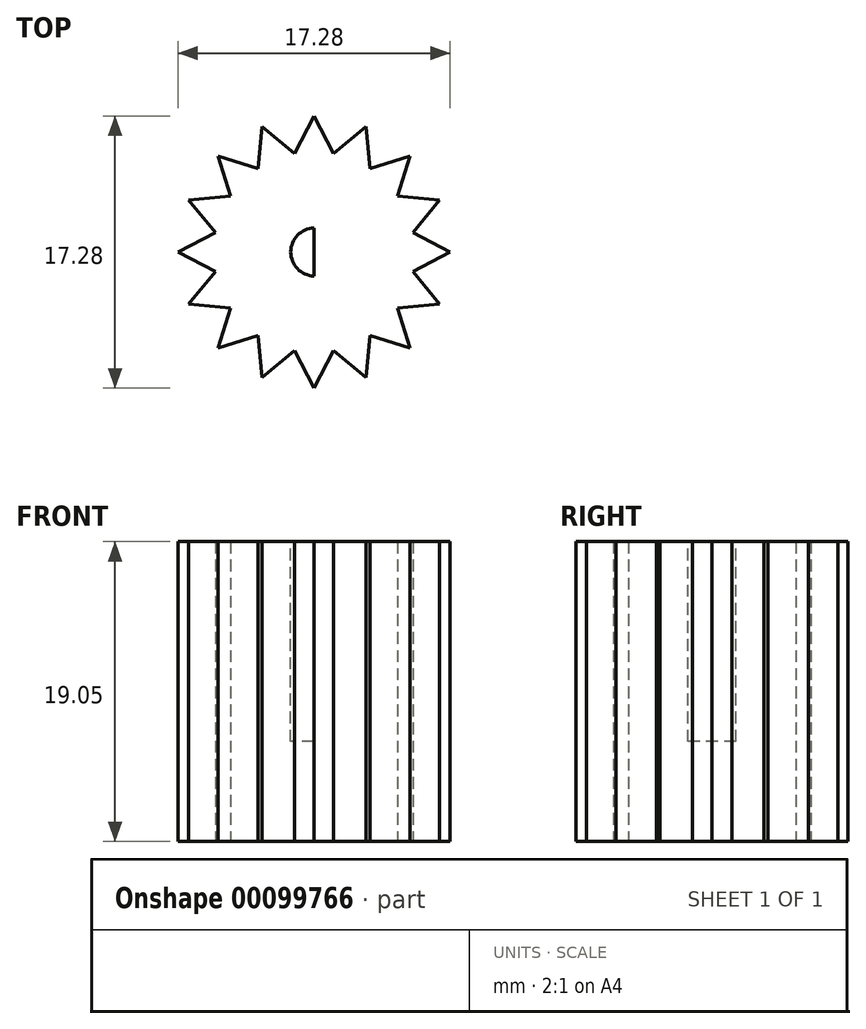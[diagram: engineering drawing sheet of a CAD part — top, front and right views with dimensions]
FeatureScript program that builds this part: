
annotation { "Feature Type Name" : "Feature", "Feature Type Description" : "" }
export const myFeature = defineFeature(function(context is Context, id is Id, definition is map)
    precondition{}
    {
        {
            var Q0;
            Q0=qCreatedBy(makeId("Top.planeOp"),FACE);
            var sketch = newSketch(context, id + "F0", { "sketchPlane" : qUnion([Q0])});
            skCircle(sketch, "E0", {"center": v(0, 0) * mm, "radius": 6.35 * mm});
            skLineSegment(sketch, "E1", {"start": v(-1.27, 6.22) * mm, "end": v(0, 8.64) * mm});
            skLineSegment(sketch, "E2", {"start": v(0, 8.64) * mm, "end": v(1.27, 6.22) * mm});
            skPoint(sketch, "E3.center", {"position": v(1.58, 1.56) * mm});
            skLineSegment(sketch, "E4.1.0", {"start": v(-3.55, 5.26) * mm, "end": v(-3.3, 7.98) * mm});
            skLineSegment(sketch, "E4.1.1", {"start": v(-3.3, 7.98) * mm, "end": v(-1.2, 6.23) * mm});
            skLineSegment(sketch, "E4.2.0", {"start": v(-5.3, 3.5) * mm, "end": v(-6.1, 6.1) * mm});
            skLineSegment(sketch, "E4.2.1", {"start": v(-6.1, 6.1) * mm, "end": v(-3.5, 5.3) * mm});
            skLineSegment(sketch, "E5.1.3.0", {"start": v(-6.23, 1.2) * mm, "end": v(-7.98, 3.3) * mm});
            skLineSegment(sketch, "E5.3.3.0", {"start": v(-7.98, 3.3) * mm, "end": v(-5.26, 3.55) * mm});
            skLineSegment(sketch, "E5.1.4.0", {"start": v(-6.22, -1.27) * mm, "end": v(-8.64, 0) * mm});
            skLineSegment(sketch, "E5.3.4.0", {"start": v(-8.64, 0) * mm, "end": v(-6.22, 1.27) * mm});
            skLineSegment(sketch, "E5.1.5.0", {"start": v(-5.26, -3.55) * mm, "end": v(-7.98, -3.3) * mm});
            skLineSegment(sketch, "E5.3.5.0", {"start": v(-7.98, -3.3) * mm, "end": v(-6.23, -1.2) * mm});
            skLineSegment(sketch, "E5.1.6.0", {"start": v(-3.5, -5.3) * mm, "end": v(-6.1, -6.1) * mm});
            skLineSegment(sketch, "E5.3.6.0", {"start": v(-6.1, -6.1) * mm, "end": v(-5.3, -3.5) * mm});
            skLineSegment(sketch, "E5.1.7.0", {"start": v(-1.2, -6.23) * mm, "end": v(-3.3, -7.98) * mm});
            skLineSegment(sketch, "E5.3.7.0", {"start": v(-3.3, -7.98) * mm, "end": v(-3.55, -5.26) * mm});
            skLineSegment(sketch, "E5.1.8.0", {"start": v(1.27, -6.22) * mm, "end": v(0, -8.64) * mm});
            skLineSegment(sketch, "E5.3.8.0", {"start": v(0, -8.64) * mm, "end": v(-1.27, -6.22) * mm});
            skLineSegment(sketch, "E5.1.9.0", {"start": v(3.55, -5.26) * mm, "end": v(3.3, -7.98) * mm});
            skLineSegment(sketch, "E5.3.9.0", {"start": v(3.3, -7.98) * mm, "end": v(1.2, -6.23) * mm});
            skLineSegment(sketch, "E5.1.10.0", {"start": v(5.3, -3.5) * mm, "end": v(6.1, -6.1) * mm});
            skLineSegment(sketch, "E5.3.10.0", {"start": v(6.1, -6.1) * mm, "end": v(3.5, -5.3) * mm});
            skLineSegment(sketch, "E5.1.11.0", {"start": v(6.23, -1.2) * mm, "end": v(7.98, -3.3) * mm});
            skLineSegment(sketch, "E5.3.11.0", {"start": v(7.98, -3.3) * mm, "end": v(5.26, -3.55) * mm});
            skLineSegment(sketch, "E6.1.12.0", {"start": v(6.22, 1.27) * mm, "end": v(8.64, 0) * mm});
            skLineSegment(sketch, "E6.3.12.0", {"start": v(8.64, 0) * mm, "end": v(6.22, -1.27) * mm});
            skLineSegment(sketch, "E6.1.13.0", {"start": v(5.26, 3.55) * mm, "end": v(7.98, 3.3) * mm});
            skLineSegment(sketch, "E6.3.13.0", {"start": v(7.98, 3.3) * mm, "end": v(6.23, 1.2) * mm});
            skLineSegment(sketch, "E7.1.14.0", {"start": v(3.5, 5.3) * mm, "end": v(6.1, 6.1) * mm});
            skLineSegment(sketch, "E7.3.14.0", {"start": v(6.1, 6.1) * mm, "end": v(5.3, 3.5) * mm});
            skLineSegment(sketch, "E7.1.15.0", {"start": v(1.2, 6.23) * mm, "end": v(3.3, 7.98) * mm});
            skLineSegment(sketch, "E7.3.15.0", {"start": v(3.3, 7.98) * mm, "end": v(3.55, 5.26) * mm});
            skSolve(sketch);
        }
        {
            var Q0;
            {var subQ3=sQuery(id+"F0.wireOp",EDGE,"E6.1.13.0");var subQ5=sQuery(id+"F0.wireOp",EDGE,"E0");var subQ6=makeQuery(id+"F0.imprint","INTERSECT",VERTEX,{"derivedFrom":[subQ5,subQ3]});Q0=makeQuery(id+"F0.imprint","IMPRINT",FACE,{"disambiguationData":[TD([[makeQuery(id+"F0.imprint","IMPRINT",EDGE,{"disambiguationData":[TD([[subQ6,-1.0]])],"derivedFrom":subQ5}),-1.0]])]});}
            var Q1;
            {var subQ3=sQuery(id+"F0.wireOp",EDGE,"E5.1.10.0");var subQ5=sQuery(id+"F0.wireOp",EDGE,"E0");var subQ6=makeQuery(id+"F0.imprint","INTERSECT",VERTEX,{"derivedFrom":[subQ5,subQ3]});Q1=makeQuery(id+"F0.imprint","IMPRINT",FACE,{"disambiguationData":[TD([[makeQuery(id+"F0.imprint","IMPRINT",EDGE,{"disambiguationData":[TD([[subQ6,-1.0]])],"derivedFrom":subQ5}),-1.0]])]});}
            var Q2;
            {var subQ3=sQuery(id+"F0.wireOp",EDGE,"E5.1.7.0");var subQ7=sQuery(id+"F0.wireOp",EDGE,"E0");var subQ8=makeQuery(id+"F0.imprint","INTERSECT",VERTEX,{"derivedFrom":[subQ7,subQ3]});Q2=makeQuery(id+"F0.imprint","IMPRINT",FACE,{"disambiguationData":[TD([[makeQuery(id+"F0.imprint","IMPRINT",EDGE,{"disambiguationData":[TD([[subQ8,-1.0]])],"derivedFrom":subQ7}),-1.0]])]});}
            var Q3;
            {var subQ3=sQuery(id+"F0.wireOp",EDGE,"E5.1.6.0");var subQ7=sQuery(id+"F0.wireOp",EDGE,"E0");var subQ9=makeQuery(id+"F0.imprint","INTERSECT",VERTEX,{"derivedFrom":[subQ7,subQ3]});Q3=makeQuery(id+"F0.imprint","IMPRINT",FACE,{"disambiguationData":[TD([[makeQuery(id+"F0.imprint","IMPRINT",EDGE,{"disambiguationData":[TD([[subQ9,-1.0]])],"derivedFrom":subQ7}),-1.0]])]});}
            var Q4;
            {var subQ0=sQuery(id+"F0.wireOp",EDGE,"E0");var subQ23=makeQuery(id+"F0.imprint","INTERSECT",VERTEX,{"derivedFrom":[subQ0,sQuery(id+"F0.wireOp",EDGE,"E6.1.12.0")]});Q4=makeQuery(id+"F0.imprint","IMPRINT",FACE,{"disambiguationData":[TD([[makeQuery(id+"F0.imprint","IMPRINT",EDGE,{"disambiguationData":[TD([[subQ23,1.0]])],"derivedFrom":subQ0}),1.0]])]});}
            var Q5;
            {var subQ3=sQuery(id+"F0.wireOp",EDGE,"E2");var subQ6=sQuery(id+"F0.wireOp",EDGE,"E0");var subQ9=makeQuery(id+"F0.imprint","INTERSECT",VERTEX,{"derivedFrom":[subQ6,subQ3]});Q5=makeQuery(id+"F0.imprint","IMPRINT",FACE,{"disambiguationData":[TD([[makeQuery(id+"F0.imprint","IMPRINT",EDGE,{"disambiguationData":[TD([[subQ9,1.0]])],"derivedFrom":subQ6}),-1.0]])]});}
            var Q6;
            {var subQ0=sQuery(id+"F0.wireOp",EDGE,"E6.1.12.0");var subQ1=sQuery(id+"F0.wireOp",EDGE,"E0");var subQ2=makeQuery(id+"F0.imprint","INTERSECT",VERTEX,{"derivedFrom":[subQ1,subQ0]});Q6=makeQuery(id+"F0.imprint","IMPRINT",FACE,{"disambiguationData":[TD([[makeQuery(id+"F0.imprint","IMPRINT",EDGE,{"disambiguationData":[TD([[subQ2,-1.0]])],"derivedFrom":subQ1}),-1.0]])]});}
            var Q7;
            {var subQ3=sQuery(id+"F0.wireOp",EDGE,"E4.2.0");var subQ5=sQuery(id+"F0.wireOp",EDGE,"E0");var subQ6=makeQuery(id+"F0.imprint","INTERSECT",VERTEX,{"derivedFrom":[subQ5,subQ3]});Q7=makeQuery(id+"F0.imprint","IMPRINT",FACE,{"disambiguationData":[TD([[makeQuery(id+"F0.imprint","IMPRINT",EDGE,{"disambiguationData":[TD([[subQ6,-1.0]])],"derivedFrom":subQ5}),-1.0]])]});}
            var Q8;
            {var subQ0=sQuery(id+"F0.wireOp",EDGE,"E5.1.9.0");var subQ1=sQuery(id+"F0.wireOp",EDGE,"E0");var subQ2=makeQuery(id+"F0.imprint","INTERSECT",VERTEX,{"derivedFrom":[subQ1,subQ0]});Q8=makeQuery(id+"F0.imprint","IMPRINT",FACE,{"disambiguationData":[TD([[makeQuery(id+"F0.imprint","IMPRINT",EDGE,{"disambiguationData":[TD([[subQ2,-1.0]])],"derivedFrom":subQ1}),-1.0]])]});}
            var Q9;
            {var subQ0=sQuery(id+"F0.wireOp",EDGE,"E4.1.1");var subQ1=sQuery(id+"F0.wireOp",EDGE,"E0");var subQ2=makeQuery(id+"F0.imprint","INTERSECT",VERTEX,{"derivedFrom":[subQ1,subQ0]});Q9=makeQuery(id+"F0.imprint","IMPRINT",FACE,{"disambiguationData":[TD([[makeQuery(id+"F0.imprint","IMPRINT",EDGE,{"disambiguationData":[TD([[subQ2,1.0]])],"derivedFrom":subQ1}),-1.0]])]});}
            var Q10;
            {var subQ3=sQuery(id+"F0.wireOp",EDGE,"E4.1.0");var subQ5=sQuery(id+"F0.wireOp",EDGE,"E0");var subQ6=makeQuery(id+"F0.imprint","INTERSECT",VERTEX,{"derivedFrom":[subQ5,subQ3]});Q10=makeQuery(id+"F0.imprint","IMPRINT",FACE,{"disambiguationData":[TD([[makeQuery(id+"F0.imprint","IMPRINT",EDGE,{"disambiguationData":[TD([[subQ6,-1.0]])],"derivedFrom":subQ5}),-1.0]])]});}
            var Q11;
            {var subQ3=sQuery(id+"F0.wireOp",EDGE,"E5.1.3.0");var subQ7=sQuery(id+"F0.wireOp",EDGE,"E0");var subQ8=makeQuery(id+"F0.imprint","INTERSECT",VERTEX,{"derivedFrom":[subQ7,subQ3]});Q11=makeQuery(id+"F0.imprint","IMPRINT",FACE,{"disambiguationData":[TD([[makeQuery(id+"F0.imprint","IMPRINT",EDGE,{"disambiguationData":[TD([[subQ8,-1.0]])],"derivedFrom":subQ7}),-1.0]])]});}
            var Q12;
            {var subQ3=sQuery(id+"F0.wireOp",EDGE,"E5.1.4.0");var subQ7=sQuery(id+"F0.wireOp",EDGE,"E0");var subQ9=makeQuery(id+"F0.imprint","INTERSECT",VERTEX,{"derivedFrom":[subQ7,subQ3]});Q12=makeQuery(id+"F0.imprint","IMPRINT",FACE,{"disambiguationData":[TD([[makeQuery(id+"F0.imprint","IMPRINT",EDGE,{"disambiguationData":[TD([[subQ9,-1.0]])],"derivedFrom":subQ7}),-1.0]])]});}
            var Q13;
            {var subQ3=sQuery(id+"F0.wireOp",EDGE,"E5.1.8.0");var subQ5=sQuery(id+"F0.wireOp",EDGE,"E0");var subQ6=makeQuery(id+"F0.imprint","INTERSECT",VERTEX,{"derivedFrom":[subQ5,subQ3]});Q13=makeQuery(id+"F0.imprint","IMPRINT",FACE,{"disambiguationData":[TD([[makeQuery(id+"F0.imprint","IMPRINT",EDGE,{"disambiguationData":[TD([[subQ6,-1.0]])],"derivedFrom":subQ5}),-1.0]])]});}
            var Q14;
            {var subQ5=sQuery(id+"F0.wireOp",EDGE,"E1");var subQ7=sQuery(id+"F0.wireOp",EDGE,"E0");var subQ8=makeQuery(id+"F0.imprint","INTERSECT",VERTEX,{"derivedFrom":[subQ7,subQ5]});Q14=makeQuery(id+"F0.imprint","IMPRINT",FACE,{"disambiguationData":[TD([[makeQuery(id+"F0.imprint","IMPRINT",EDGE,{"disambiguationData":[TD([[subQ8,-1.0]])],"derivedFrom":subQ7}),-1.0]])]});}
            var Q15;
            {var subQ3=sQuery(id+"F0.wireOp",EDGE,"E5.1.5.0");var subQ7=sQuery(id+"F0.wireOp",EDGE,"E0");var subQ8=makeQuery(id+"F0.imprint","INTERSECT",VERTEX,{"derivedFrom":[subQ7,subQ3]});Q15=makeQuery(id+"F0.imprint","IMPRINT",FACE,{"disambiguationData":[TD([[makeQuery(id+"F0.imprint","IMPRINT",EDGE,{"disambiguationData":[TD([[subQ8,-1.0]])],"derivedFrom":subQ7}),-1.0]])]});}
            var Q16;
            {var subQ3=sQuery(id+"F0.wireOp",EDGE,"E5.1.11.0");var subQ5=sQuery(id+"F0.wireOp",EDGE,"E0");var subQ6=makeQuery(id+"F0.imprint","INTERSECT",VERTEX,{"derivedFrom":[subQ5,subQ3]});Q16=makeQuery(id+"F0.imprint","IMPRINT",FACE,{"disambiguationData":[TD([[makeQuery(id+"F0.imprint","IMPRINT",EDGE,{"disambiguationData":[TD([[subQ6,-1.0]])],"derivedFrom":subQ5}),-1.0]])]});}
            var Q17;
            {var subQ0=sQuery(id+"F0.wireOp",EDGE,"E4.1.0");var subQ1=sQuery(id+"F0.wireOp",EDGE,"E0");var subQ2=makeQuery(id+"F0.imprint","INTERSECT",VERTEX,{"derivedFrom":[subQ1,subQ0]});Q17=makeQuery(id+"F0.imprint","IMPRINT",FACE,{"disambiguationData":[TD([[makeQuery(id+"F0.imprint","IMPRINT",EDGE,{"disambiguationData":[TD([[subQ2,1.0]])],"derivedFrom":subQ1}),-1.0]])]});}
            var Q18;
            {var subQ0=sQuery(id+"F0.wireOp",EDGE,"E5.1.6.0");var subQ1=sQuery(id+"F0.wireOp",EDGE,"E0");var subQ2=makeQuery(id+"F0.imprint","INTERSECT",VERTEX,{"derivedFrom":[subQ1,subQ0]});Q18=makeQuery(id+"F0.imprint","IMPRINT",FACE,{"disambiguationData":[TD([[makeQuery(id+"F0.imprint","IMPRINT",EDGE,{"disambiguationData":[TD([[subQ2,1.0]])],"derivedFrom":subQ1}),-1.0]])]});}
            var Q19;
            {var subQ0=sQuery(id+"F0.wireOp",EDGE,"E7.1.14.0");var subQ1=sQuery(id+"F0.wireOp",EDGE,"E0");var subQ2=makeQuery(id+"F0.imprint","INTERSECT",VERTEX,{"derivedFrom":[subQ1,subQ0]});Q19=makeQuery(id+"F0.imprint","IMPRINT",FACE,{"disambiguationData":[TD([[makeQuery(id+"F0.imprint","IMPRINT",EDGE,{"disambiguationData":[TD([[subQ2,1.0]])],"derivedFrom":subQ1}),-1.0]])]});}
            var Q20;
            {var subQ0=sQuery(id+"F0.wireOp",EDGE,"E5.1.7.0");var subQ1=sQuery(id+"F0.wireOp",EDGE,"E0");var subQ2=makeQuery(id+"F0.imprint","INTERSECT",VERTEX,{"derivedFrom":[subQ1,subQ0]});Q20=makeQuery(id+"F0.imprint","IMPRINT",FACE,{"disambiguationData":[TD([[makeQuery(id+"F0.imprint","IMPRINT",EDGE,{"disambiguationData":[TD([[subQ2,1.0]])],"derivedFrom":subQ1}),-1.0]])]});}
            var Q21;
            {var subQ0=sQuery(id+"F0.wireOp",EDGE,"E5.1.10.0");var subQ1=sQuery(id+"F0.wireOp",EDGE,"E0");var subQ2=makeQuery(id+"F0.imprint","INTERSECT",VERTEX,{"derivedFrom":[subQ1,subQ0]});Q21=makeQuery(id+"F0.imprint","IMPRINT",FACE,{"disambiguationData":[TD([[makeQuery(id+"F0.imprint","IMPRINT",EDGE,{"disambiguationData":[TD([[subQ2,1.0]])],"derivedFrom":subQ1}),-1.0]])]});}
            var Q22;
            {var subQ0=sQuery(id+"F0.wireOp",EDGE,"E2");var subQ1=sQuery(id+"F0.wireOp",EDGE,"E0");var subQ2=makeQuery(id+"F0.imprint","INTERSECT",VERTEX,{"derivedFrom":[subQ1,subQ0]});Q22=makeQuery(id+"F0.imprint","IMPRINT",FACE,{"disambiguationData":[TD([[makeQuery(id+"F0.imprint","IMPRINT",EDGE,{"disambiguationData":[TD([[subQ2,-1.0]])],"derivedFrom":subQ1}),-1.0]])]});}
            var Q23;
            {var subQ0=sQuery(id+"F0.wireOp",EDGE,"E4.2.0");var subQ1=sQuery(id+"F0.wireOp",EDGE,"E0");var subQ2=makeQuery(id+"F0.imprint","INTERSECT",VERTEX,{"derivedFrom":[subQ1,subQ0]});Q23=makeQuery(id+"F0.imprint","IMPRINT",FACE,{"disambiguationData":[TD([[makeQuery(id+"F0.imprint","IMPRINT",EDGE,{"disambiguationData":[TD([[subQ2,1.0]])],"derivedFrom":subQ1}),-1.0]])]});}
            var Q24;
            {var subQ0=sQuery(id+"F0.wireOp",EDGE,"E6.1.12.0");var subQ1=sQuery(id+"F0.wireOp",EDGE,"E0");var subQ2=makeQuery(id+"F0.imprint","INTERSECT",VERTEX,{"derivedFrom":[subQ1,subQ0]});Q24=makeQuery(id+"F0.imprint","IMPRINT",FACE,{"disambiguationData":[TD([[makeQuery(id+"F0.imprint","IMPRINT",EDGE,{"disambiguationData":[TD([[subQ2,1.0]])],"derivedFrom":subQ1}),-1.0]])]});}
            var Q25;
            {var subQ0=sQuery(id+"F0.wireOp",EDGE,"E5.1.4.0");var subQ1=sQuery(id+"F0.wireOp",EDGE,"E0");var subQ2=makeQuery(id+"F0.imprint","INTERSECT",VERTEX,{"derivedFrom":[subQ1,subQ0]});Q25=makeQuery(id+"F0.imprint","IMPRINT",FACE,{"disambiguationData":[TD([[makeQuery(id+"F0.imprint","IMPRINT",EDGE,{"disambiguationData":[TD([[subQ2,1.0]])],"derivedFrom":subQ1}),-1.0]])]});}
            var Q26;
            {var subQ0=sQuery(id+"F0.wireOp",EDGE,"E6.1.13.0");var subQ1=sQuery(id+"F0.wireOp",EDGE,"E0");var subQ2=makeQuery(id+"F0.imprint","INTERSECT",VERTEX,{"derivedFrom":[subQ1,subQ0]});Q26=makeQuery(id+"F0.imprint","IMPRINT",FACE,{"disambiguationData":[TD([[makeQuery(id+"F0.imprint","IMPRINT",EDGE,{"disambiguationData":[TD([[subQ2,1.0]])],"derivedFrom":subQ1}),-1.0]])]});}
            var Q27;
            {var subQ0=sQuery(id+"F0.wireOp",EDGE,"E1");var subQ1=sQuery(id+"F0.wireOp",EDGE,"E0");var subQ2=makeQuery(id+"F0.imprint","INTERSECT",VERTEX,{"derivedFrom":[subQ1,subQ0]});Q27=makeQuery(id+"F0.imprint","IMPRINT",FACE,{"disambiguationData":[TD([[makeQuery(id+"F0.imprint","IMPRINT",EDGE,{"disambiguationData":[TD([[subQ2,1.0]])],"derivedFrom":subQ1}),-1.0]])]});}
            var Q28;
            {var subQ0=sQuery(id+"F0.wireOp",EDGE,"E5.1.8.0");var subQ1=sQuery(id+"F0.wireOp",EDGE,"E0");var subQ2=makeQuery(id+"F0.imprint","INTERSECT",VERTEX,{"derivedFrom":[subQ1,subQ0]});Q28=makeQuery(id+"F0.imprint","IMPRINT",FACE,{"disambiguationData":[TD([[makeQuery(id+"F0.imprint","IMPRINT",EDGE,{"disambiguationData":[TD([[subQ2,1.0]])],"derivedFrom":subQ1}),-1.0]])]});}
            var Q29;
            {var subQ0=sQuery(id+"F0.wireOp",EDGE,"E5.1.3.0");var subQ1=sQuery(id+"F0.wireOp",EDGE,"E0");var subQ2=makeQuery(id+"F0.imprint","INTERSECT",VERTEX,{"derivedFrom":[subQ1,subQ0]});Q29=makeQuery(id+"F0.imprint","IMPRINT",FACE,{"disambiguationData":[TD([[makeQuery(id+"F0.imprint","IMPRINT",EDGE,{"disambiguationData":[TD([[subQ2,1.0]])],"derivedFrom":subQ1}),-1.0]])]});}
            var Q30;
            {var subQ0=sQuery(id+"F0.wireOp",EDGE,"E5.1.11.0");var subQ1=sQuery(id+"F0.wireOp",EDGE,"E0");var subQ2=makeQuery(id+"F0.imprint","INTERSECT",VERTEX,{"derivedFrom":[subQ1,subQ0]});Q30=makeQuery(id+"F0.imprint","IMPRINT",FACE,{"disambiguationData":[TD([[makeQuery(id+"F0.imprint","IMPRINT",EDGE,{"disambiguationData":[TD([[subQ2,1.0]])],"derivedFrom":subQ1}),-1.0]])]});}
            var Q31;
            {var subQ0=sQuery(id+"F0.wireOp",EDGE,"E5.1.9.0");var subQ1=sQuery(id+"F0.wireOp",EDGE,"E0");var subQ2=makeQuery(id+"F0.imprint","INTERSECT",VERTEX,{"derivedFrom":[subQ1,subQ0]});Q31=makeQuery(id+"F0.imprint","IMPRINT",FACE,{"disambiguationData":[TD([[makeQuery(id+"F0.imprint","IMPRINT",EDGE,{"disambiguationData":[TD([[subQ2,1.0]])],"derivedFrom":subQ1}),-1.0]])]});}
            var Q32;
            {var subQ0=sQuery(id+"F0.wireOp",EDGE,"E5.1.5.0");var subQ1=sQuery(id+"F0.wireOp",EDGE,"E0");var subQ2=makeQuery(id+"F0.imprint","INTERSECT",VERTEX,{"derivedFrom":[subQ1,subQ0]});Q32=makeQuery(id+"F0.imprint","IMPRINT",FACE,{"disambiguationData":[TD([[makeQuery(id+"F0.imprint","IMPRINT",EDGE,{"disambiguationData":[TD([[subQ2,1.0]])],"derivedFrom":subQ1}),-1.0]])]});}
            extrude(context, id + "F1", {"entities" : qUnion([Q0, Q1, Q2, Q3, Q4, Q5, Q6, Q7, Q8, Q9, Q10, Q11, Q12, Q13, Q14, Q15, Q16, Q17, Q18, Q19, Q20, Q21, Q22, Q23, Q24, Q25, Q26, Q27, Q28, Q29, Q30, Q31, Q32]), "depth" : 19.05 * mm});
        }
        {
            var Q0;
            Q0=makeQuery(id+"F1.opExtrude","CAP_FACE",FACE,{"disambiguationData":[OSD([sQuery(id+"F0.wireOp",EDGE,"E1"),sQuery(id+"F0.wireOp",EDGE,"E2"),sQuery(id+"F0.wireOp",EDGE,"E4.1.0"),sQuery(id+"F0.wireOp",EDGE,"E4.1.1"),sQuery(id+"F0.wireOp",EDGE,"E4.2.0"),sQuery(id+"F0.wireOp",EDGE,"E4.2.1"),sQuery(id+"F0.wireOp",EDGE,"E5.1.3.0"),sQuery(id+"F0.wireOp",EDGE,"E5.3.3.0"),sQuery(id+"F0.wireOp",EDGE,"E5.1.4.0"),sQuery(id+"F0.wireOp",EDGE,"E5.3.4.0"),sQuery(id+"F0.wireOp",EDGE,"E5.1.5.0"),sQuery(id+"F0.wireOp",EDGE,"E5.3.5.0"),sQuery(id+"F0.wireOp",EDGE,"E5.1.6.0"),sQuery(id+"F0.wireOp",EDGE,"E5.3.6.0"),sQuery(id+"F0.wireOp",EDGE,"E5.1.7.0"),sQuery(id+"F0.wireOp",EDGE,"E5.3.7.0"),sQuery(id+"F0.wireOp",EDGE,"E5.1.8.0"),sQuery(id+"F0.wireOp",EDGE,"E5.3.8.0"),sQuery(id+"F0.wireOp",EDGE,"E5.1.9.0"),sQuery(id+"F0.wireOp",EDGE,"E5.3.9.0"),sQuery(id+"F0.wireOp",EDGE,"E5.1.10.0"),sQuery(id+"F0.wireOp",EDGE,"E5.3.10.0"),sQuery(id+"F0.wireOp",EDGE,"E5.1.11.0"),sQuery(id+"F0.wireOp",EDGE,"E5.3.11.0"),sQuery(id+"F0.wireOp",EDGE,"E6.1.12.0"),sQuery(id+"F0.wireOp",EDGE,"E6.3.12.0"),sQuery(id+"F0.wireOp",EDGE,"E6.1.13.0"),sQuery(id+"F0.wireOp",EDGE,"E6.3.13.0"),sQuery(id+"F0.wireOp",EDGE,"E7.1.14.0"),sQuery(id+"F0.wireOp",EDGE,"E7.3.14.0"),sQuery(id+"F0.wireOp",EDGE,"E7.1.15.0"),sQuery(id+"F0.wireOp",EDGE,"E7.3.15.0")])],"isStart":false});
            var sketch = newSketch(context, id + "F2", { "sketchPlane" : qUnion([Q0])});
            skCircle(sketch, "E8", {"center": v(0, 0) * mm, "radius": 1.52 * mm});
            skArc(sketch, "E9", {"start": v(0, 1.52) * mm, "mid": v(-1.48, 0) * mm, "end": v(0, -1.52) * mm});
            skLineSegment(sketch, "E10", {"start": v(0, 1.52) * mm, "end": v(0, -1.52) * mm});
            skSolve(sketch);
        }
        {
            var Q0;
            Q0=makeQuery(id+"F2.imprint","IMPRINT",FACE,{"disambiguationData":[TD([[makeQuery(id+"F2.imprint","IMPRINT",EDGE,{"derivedFrom":sQuery(id+"F2.wireOp",EDGE,"E9")}),1.0]])]});
            extrude(context, id + "F3", {"entities" : qUnion([Q0]), "operationType" : NewBodyOperationType.REMOVE, "oppositeDirection" : true, "depth" : 12.7 * mm});
        }
    });
